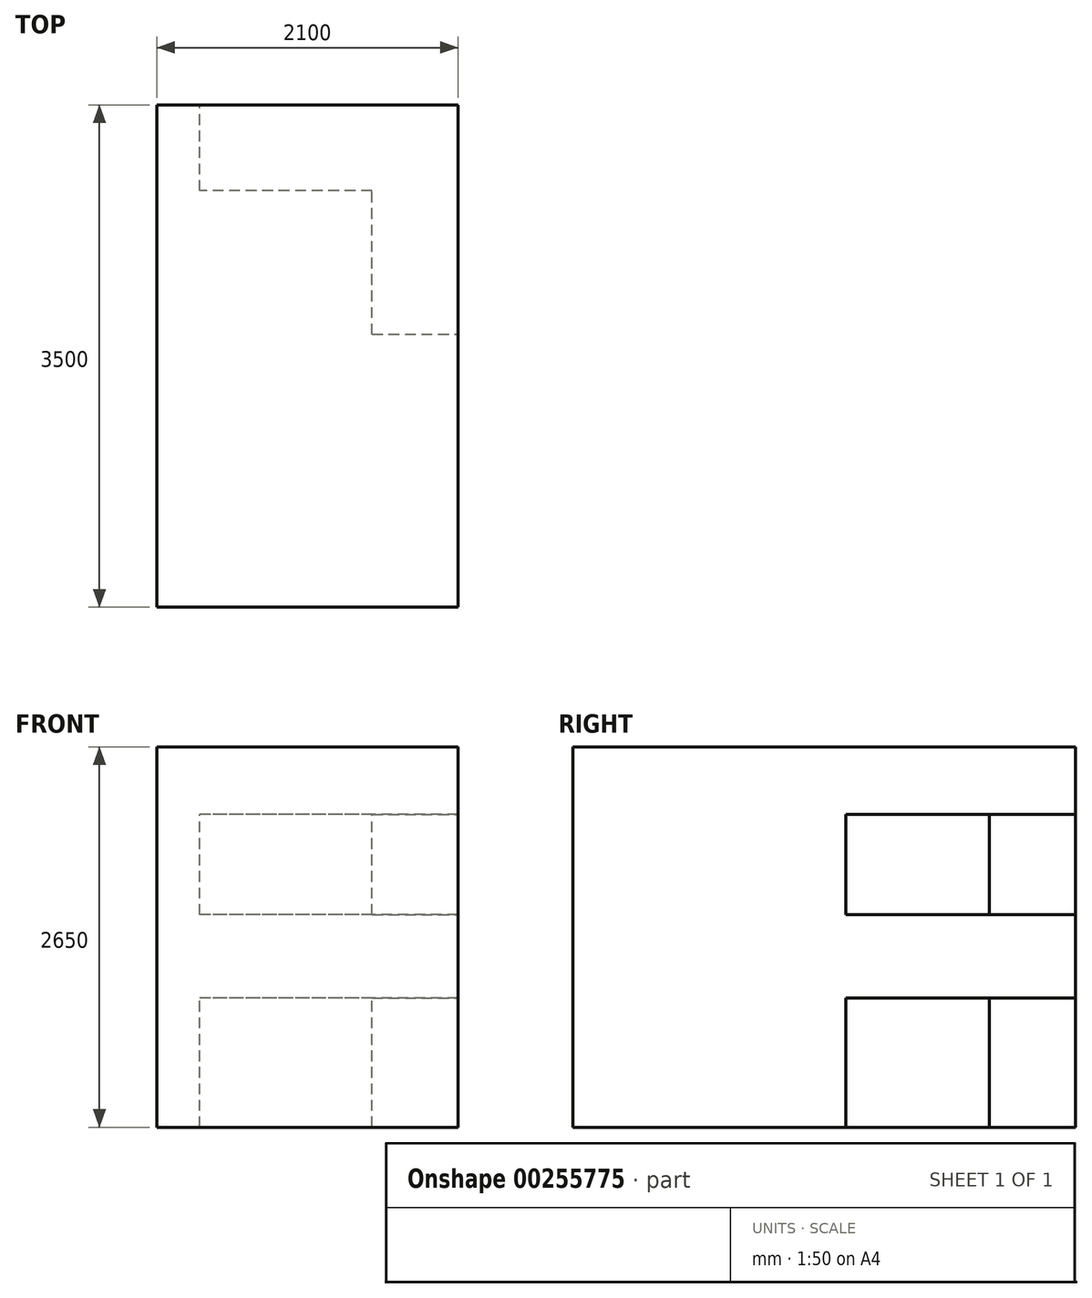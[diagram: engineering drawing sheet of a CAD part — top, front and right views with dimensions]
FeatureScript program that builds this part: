
annotation { "Feature Type Name" : "Feature", "Feature Type Description" : "" }
export const myFeature = defineFeature(function(context is Context, id is Id, definition is map)
    precondition{}
    {
        {
            var Q0;
            Q0=qCreatedBy(makeId("Front.planeOp"),FACE);
            var sketch = newSketch(context, id + "F0", { "sketchPlane" : qUnion([Q0])});
            skLineSegment(sketch, "E0.bottom", {"start": v(1050, -1325) * mm, "end": v(-1050, -1325) * mm});
            skLineSegment(sketch, "E0.top", {"start": v(1050, 1325) * mm, "end": v(-1050, 1325) * mm});
            skLineSegment(sketch, "E0.left", {"start": v(1050, -1325) * mm, "end": v(1050, 1325) * mm});
            skLineSegment(sketch, "E0.right", {"start": v(-1050, -1325) * mm, "end": v(-1050, 1325) * mm});
            skPoint(sketch, "E0.middle", {"position": v(0, 0) * mm});
            skSolve(sketch);
        }
        {
            var Q0;
            Q0 = qSketchRegion(id + "F0", true);
            extrude(context, id + "F1", {"entities" : qUnion([Q0]), "endBound" : BoundingType.SYMMETRIC, "depth" : 3500 * mm});
        }
        {
            var Q0;
            Q0=makeQuery(id+"F1.opExtrude","SWEPT_FACE",FACE,{"disambiguationData":[OSD([sQuery(id+"F0.wireOp",EDGE,"E0.left")])]});
            var sketch = newSketch(context, id + "F2", { "sketchPlane" : qUnion([Q0])});
            skLineSegment(sketch, "E1.bottom", {"start": v(1460, 952.03) * mm, "end": v(1240, 952.03) * mm});
            skLineSegment(sketch, "E1.top", {"start": v(1460, 1252.03) * mm, "end": v(1240, 1252.03) * mm});
            skLineSegment(sketch, "E1.left", {"start": v(1460, 952.03) * mm, "end": v(1460, 1252.03) * mm});
            skLineSegment(sketch, "E1.right", {"start": v(1240, 952.03) * mm, "end": v(1240, 1252.03) * mm});
            skPoint(sketch, "E1.middle", {"position": v(1350, 1102.03) * mm});
            skSolve(sketch);
        }
        {
            var Q0;
            Q0=makeQuery(id+"F1.opExtrude","SWEPT_FACE",FACE,{"disambiguationData":[OSD([sQuery(id+"F0.wireOp",EDGE,"E0.right")])]});
            var sketch = newSketch(context, id + "F3", { "sketchPlane" : qUnion([Q0])});
            skLineSegment(sketch, "E2.bottom", {"start": v(-850, 875) * mm, "end": v(650, 875) * mm});
            skLineSegment(sketch, "E2.top", {"start": v(-850, -525) * mm, "end": v(650, -525) * mm});
            skLineSegment(sketch, "E2.left", {"start": v(-850, 875) * mm, "end": v(-850, -525) * mm});
            skLineSegment(sketch, "E2.right", {"start": v(650, 875) * mm, "end": v(650, -525) * mm});
            skSolve(sketch);
        }
        {
            var Q0;
            {var subQ0=sQuery(id+"F0.wireOp",EDGE,"E0.left");var subQ1=makeQuery(id+"F1.opExtrude","SWEPT_FACE",FACE,{"disambiguationData":[OSD([subQ0])]});Q0=makeQuery(id+"FiHPxjdUDEayGbe_1.opSplitFace","SPLIT",FACE,{"disambiguationData":[TD([[makeQuery(id+"F1.opExtrude","CAP_EDGE",EDGE,{"disambiguationData":[OSD([subQ0])],"isStart":true}),1.0]])],"derivedFrom":subQ1});}
            var sketch = newSketch(context, id + "F4", { "sketchPlane" : qUnion([Q0])});
            skLineSegment(sketch, "E3.bottom", {"start": v(-350, -1325) * mm, "end": v(-1050, -1325) * mm});
            skLineSegment(sketch, "E3.top", {"start": v(-350, 675) * mm, "end": v(-1050, 675) * mm});
            skLineSegment(sketch, "E3.left", {"start": v(-350, -1325) * mm, "end": v(-350, 675) * mm});
            skLineSegment(sketch, "E3.right", {"start": v(-1050, -1325) * mm, "end": v(-1050, 675) * mm});
            skSolve(sketch);
        }
        {
            var Q0;
            Q0=makeQuery(id+"F1.opExtrude","CAP_FACE",FACE,{"disambiguationData":[OSD([sQuery(id+"F0.wireOp",EDGE,"E0.bottom"),sQuery(id+"F0.wireOp",EDGE,"E0.top"),sQuery(id+"F0.wireOp",EDGE,"E0.left"),sQuery(id+"F0.wireOp",EDGE,"E0.right")])],"isStart":true});
            var sketch = newSketch(context, id + "F5", { "sketchPlane" : qUnion([Q0])});
            skLineSegment(sketch, "E4.bottom", {"start": v(-1050, -1325) * mm, "end": v(750, -1325) * mm});
            skLineSegment(sketch, "E4.top", {"start": v(-1050, -425) * mm, "end": v(750, -425) * mm});
            skLineSegment(sketch, "E4.left", {"start": v(-1050, -1325) * mm, "end": v(-1050, -425) * mm});
            skLineSegment(sketch, "E4.right", {"start": v(750, -1325) * mm, "end": v(750, -425) * mm});
            skLineSegment(sketch, "E5.bottom", {"start": v(-1050, 155) * mm, "end": v(750, 155) * mm});
            skLineSegment(sketch, "E5.top", {"start": v(-1050, 855) * mm, "end": v(750, 855) * mm});
            skLineSegment(sketch, "E5.left", {"start": v(-1050, 155) * mm, "end": v(-1050, 855) * mm});
            skLineSegment(sketch, "E5.right", {"start": v(750, 155) * mm, "end": v(750, 855) * mm});
            skSolve(sketch);
        }
        {
            var Q0;
            Q0=makeQuery(id+"F5.imprint","IMPRINT",FACE,{"disambiguationData":[TD([[makeQuery(id+"F5.imprint","IMPRINT",EDGE,{"derivedFrom":sQuery(id+"F5.wireOp",EDGE,"E4.bottom")}),1.0]])]});
            var Q1;
            Q1=makeQuery(id+"F5.imprint","IMPRINT",FACE,{"disambiguationData":[TD([[makeQuery(id+"F5.imprint","IMPRINT",EDGE,{"derivedFrom":sQuery(id+"F5.wireOp",EDGE,"E5.bottom")}),1.0]])]});
            extrude(context, id + "F6", {"entities" : qUnion([Q0, Q1]), "operationType" : NewBodyOperationType.REMOVE, "oppositeDirection" : true, "depth" : 600 * mm, "offsetDistance" : 25 * mm});
        }
        {
            var Q0;
            {var subQ0=sQuery(id+"F0.wireOp",EDGE,"E0.left");var subQ2=makeQuery(id+"F1.opExtrude","SWEPT_FACE",FACE,{"disambiguationData":[OSD([subQ0])]});var subQ4=makeQuery(id+"F1.opExtrude","CAP_EDGE",EDGE,{"disambiguationData":[OSD([subQ0])],"isStart":true});var subQ8=makeQuery(id+"FiHPxjdUDEayGbe_1.opSplitFace","SPLIT",FACE,{"disambiguationData":[TD([[subQ4,1.0]])],"derivedFrom":subQ2});Q0=makeQuery(id+"FLNhf1OBP414KwP_1.opSplitFace","SPLIT",FACE,{"disambiguationData":[TD([[subQ4,1.0]])],"derivedFrom":subQ8});}
            var sketch = newSketch(context, id + "F7", { "sketchPlane" : qUnion([Q0])});
            skLineSegment(sketch, "E6.bottom", {"start": v(1150, -1325) * mm, "end": v(150, -1325) * mm});
            skLineSegment(sketch, "E6.top", {"start": v(1150, -425) * mm, "end": v(150, -425) * mm});
            skLineSegment(sketch, "E6.left", {"start": v(1150, -1325) * mm, "end": v(1150, -425) * mm});
            skLineSegment(sketch, "E6.right", {"start": v(150, -1325) * mm, "end": v(150, -425) * mm});
            skLineSegment(sketch, "E7.bottom", {"start": v(1150, 155) * mm, "end": v(150, 155) * mm});
            skLineSegment(sketch, "E7.top", {"start": v(1150, 855) * mm, "end": v(150, 855) * mm});
            skLineSegment(sketch, "E7.left", {"start": v(1150, 155) * mm, "end": v(1150, 855) * mm});
            skLineSegment(sketch, "E7.right", {"start": v(150, 155) * mm, "end": v(150, 855) * mm});
            skSolve(sketch);
        }
        {
            var Q0;
            Q0 = qSketchRegion(id + "F7", true);
            extrude(context, id + "F8", {"entities" : qUnion([Q0]), "operationType" : NewBodyOperationType.REMOVE, "oppositeDirection" : true, "depth" : 600 * mm, "offsetDistance" : 25 * mm});
        }
    });
